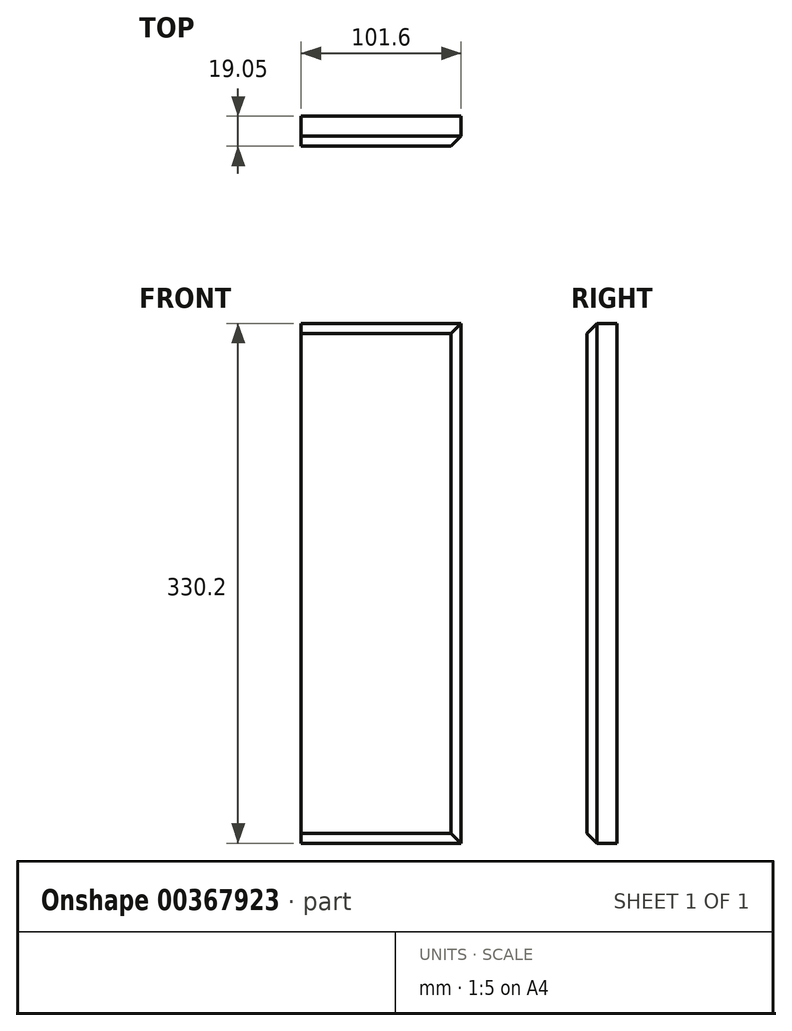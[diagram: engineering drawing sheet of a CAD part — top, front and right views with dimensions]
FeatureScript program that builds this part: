
annotation { "Feature Type Name" : "Feature", "Feature Type Description" : "" }
export const myFeature = defineFeature(function(context is Context, id is Id, definition is map)
    precondition{}
    {
        {
            var Q0;
            Q0=qCreatedBy(makeId("Front.planeOp"),FACE);
            var sketch = newSketch(context, id + "F0", { "sketchPlane" : qUnion([Q0])});
            skLineSegment(sketch, "E0.bottom", {"start": v(-65.39, 161.04) * mm, "end": v(36.21, 161.04) * mm});
            skLineSegment(sketch, "E0.top", {"start": v(-65.39, -169.16) * mm, "end": v(36.21, -169.16) * mm});
            skLineSegment(sketch, "E0.left", {"start": v(-65.39, 161.04) * mm, "end": v(-65.39, -169.16) * mm});
            skLineSegment(sketch, "E0.right", {"start": v(36.21, 161.04) * mm, "end": v(36.21, -169.16) * mm});
            skSolve(sketch);
        }
        {
            var Q0;
            Q0=makeQuery(id+"F0.imprint","IMPRINT",FACE,{"disambiguationData":[TD([[makeQuery(id+"F0.imprint","IMPRINT",EDGE,{"derivedFrom":sQuery(id+"F0.wireOp",EDGE,"E0.bottom")}),-1.0]])]});
            extrude(context, id + "F1", {"entities" : qUnion([Q0]), "depth" : 19.05 * mm});
        }
        {
            var Q0;
            Q0=makeQuery(id+"F1.opExtrude","CAP_EDGE",EDGE,{"disambiguationData":[OSD([sQuery(id+"F0.wireOp",EDGE,"E0.top")])],"isStart":false});
            var Q1;
            Q1=makeQuery(id+"F1.opExtrude","CAP_EDGE",EDGE,{"disambiguationData":[OSD([sQuery(id+"F0.wireOp",EDGE,"E0.right")])],"isStart":false});
            var Q2;
            Q2=makeQuery(id+"F1.opExtrude","CAP_EDGE",EDGE,{"disambiguationData":[OSD([sQuery(id+"F0.wireOp",EDGE,"E0.bottom")])],"isStart":false});
            chamfer(context, id + "F2", {"entities" : qUnion([Q0, Q1, Q2]), "width" : 6.35 * mm, "tangentPropagation" : true});
        }
    });
